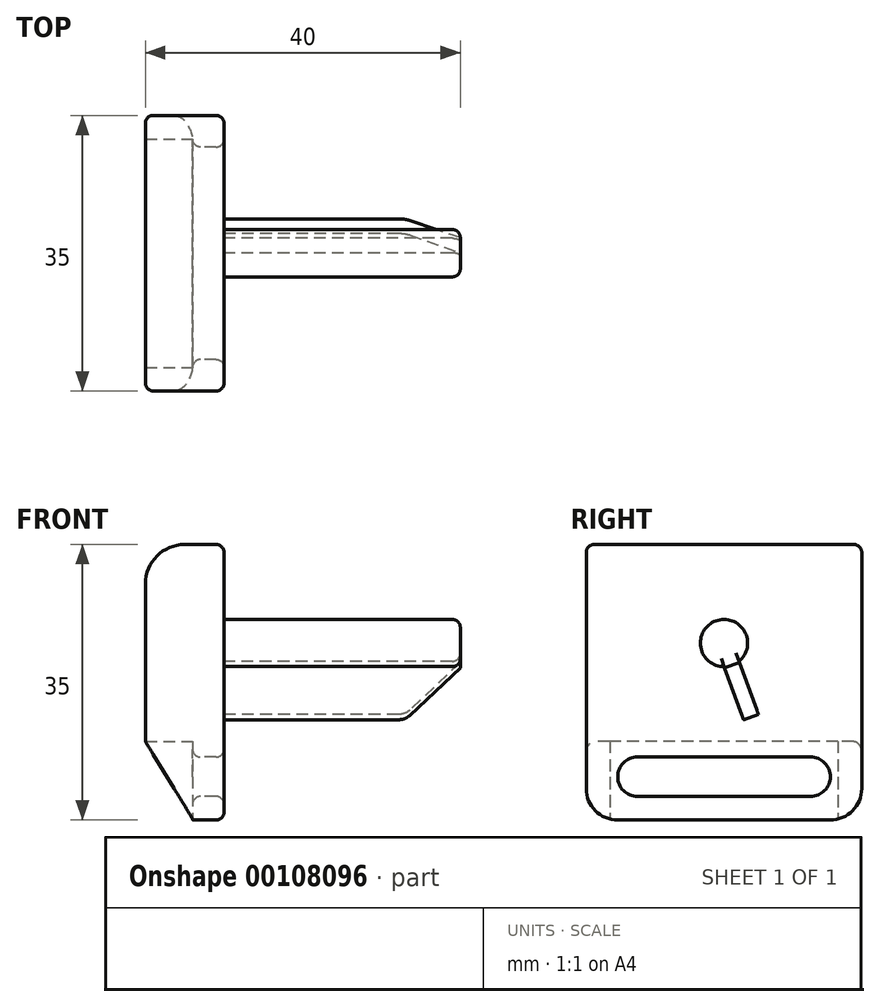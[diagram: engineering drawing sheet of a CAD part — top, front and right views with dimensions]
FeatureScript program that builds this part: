
annotation { "Feature Type Name" : "Feature", "Feature Type Description" : "" }
export const myFeature = defineFeature(function(context is Context, id is Id, definition is map)
    precondition{}
    {
        {
            var Q0;
            Q0=qCreatedBy(makeId("Right.planeOp"),FACE);
            var sketch = newSketch(context, id + "F0", { "sketchPlane" : qUnion([Q0])});
            skLineSegment(sketch, "E0.bottom", {"start": v(17.5, 12.5) * mm, "end": v(-17.5, 12.5) * mm});
            skLineSegment(sketch, "E0.top", {"start": v(17.5, -12.5) * mm, "end": v(-17.5, -12.5) * mm});
            skLineSegment(sketch, "E0.left", {"start": v(17.5, 12.5) * mm, "end": v(17.5, -12.5) * mm});
            skLineSegment(sketch, "E0.right", {"start": v(-17.5, 12.5) * mm, "end": v(-17.5, -12.5) * mm});
            skPoint(sketch, "E0.middle", {"position": v(0, 0) * mm});
            skSolve(sketch);
        }
        {
            var Q0;
            Q0 = qSketchRegion(id + "F0", true);
            extrude(context, id + "F1", {"entities" : qUnion([Q0]), "depth" : 6 * mm, "offsetDistance" : 25 * mm});
        }
        {
            var Q0;
            Q0=makeQuery(id+"F1.opExtrude","CAP_FACE",FACE,{"disambiguationData":[OSD([sQuery(id+"F0.wireOp",EDGE,"E0.bottom"),sQuery(id+"F0.wireOp",EDGE,"E0.top"),sQuery(id+"F0.wireOp",EDGE,"E0.left"),sQuery(id+"F0.wireOp",EDGE,"E0.right")])],"isStart":false});
            var sketch = newSketch(context, id + "F2", { "sketchPlane" : qUnion([Q0])});
            skPoint(sketch, "E1.0", {"position": v(-17.5, 12.5) * mm});
            skPoint(sketch, "E1.1", {"position": v(17.5, 12.5) * mm});
            skLineSegment(sketch, "E2.bottom", {"start": v(-17.5, 12.5) * mm, "end": v(17.5, 12.5) * mm});
            skLineSegment(sketch, "E2.top", {"start": v(-13.5, -22.5) * mm, "end": v(13.5, -22.5) * mm});
            skLineSegment(sketch, "E2.left", {"start": v(-17.5, 12.5) * mm, "end": v(-17.5, -18.5) * mm});
            skLineSegment(sketch, "E2.right", {"start": v(17.5, 12.5) * mm, "end": v(17.5, -18.5) * mm});
            skPoint(sketch, "E3.visualSharp", {"position": v(-17.5, -22.5) * mm});
            skArc(sketch, "E3.filletArc", {"start": v(-17.5, -18.5) * mm, "mid": v(-16.33, -21.33) * mm, "end": v(-13.5, -22.5) * mm});
            skPoint(sketch, "E4.visualSharp", {"position": v(17.5, -22.5) * mm});
            skArc(sketch, "E4.filletArc", {"start": v(13.5, -22.5) * mm, "mid": v(16.33, -21.33) * mm, "end": v(17.5, -18.5) * mm});
            skArc(sketch, "E5", {"start": v(-11, -14.5) * mm, "mid": v(-13.5, -17) * mm, "end": v(-11, -19.5) * mm});
            skArc(sketch, "E6.MirrorC", {"start": v(11, -14.5) * mm, "mid": v(13.5, -17) * mm, "end": v(11, -19.5) * mm});
            skLineSegment(sketch, "E7", {"start": v(-11, -14.5) * mm, "end": v(11, -14.5) * mm});
            skLineSegment(sketch, "E8", {"start": v(-11, -19.5) * mm, "end": v(11, -19.5) * mm});
            skSolve(sketch);
        }
        {
            var Q0;
            Q0 = qSketchRegion(id + "F2", true);
            extrude(context, id + "F3", {"entities" : qUnion([Q0]), "operationType" : NewBodyOperationType.ADD, "depth" : 4 * mm, "offsetDistance" : 25 * mm});
        }
        {
            var Q0;
            Q0=makeQuery(id+"F3.opExtrude","CAP_EDGE",EDGE,{"disambiguationData":[OSD([sQuery(id+"F2.wireOp",EDGE,"E3.filletArc")])],"isStart":false});
            var Q1;
            Q1=makeQuery(id+"F3.opExtrude","CAP_EDGE",EDGE,{"disambiguationData":[OSD([sQuery(id+"F2.wireOp",EDGE,"E8")])],"isStart":false});
            var Q2;
            Q2=makeQuery(id+"F3.opExtrude","CAP_EDGE",EDGE,{"disambiguationData":[OSD([sQuery(id+"F2.wireOp",EDGE,"E8")])],"isStart":true});
            fillet(context, id + "F4", {"entities" : qUnion([Q0, Q1, Q2]), "tangentPropagation" : true, "radius" : 1 * mm, "defaultsChanged" : false, "vertexSettings" : [], "allowEdgeOverflow" : false});
        }
        {
            var Q0;
            Q0=makeQuery(id+"F3.opExtrude","CAP_FACE",FACE,{"disambiguationData":[OSD([sQuery(id+"F2.wireOp",EDGE,"E2.bottom"),sQuery(id+"F2.wireOp",EDGE,"E2.top"),sQuery(id+"F2.wireOp",EDGE,"E2.left"),sQuery(id+"F2.wireOp",EDGE,"E2.right"),sQuery(id+"F2.wireOp",EDGE,"E3.filletArc"),sQuery(id+"F2.wireOp",EDGE,"E4.filletArc"),sQuery(id+"F2.wireOp",EDGE,"E5"),sQuery(id+"F2.wireOp",EDGE,"E6.MirrorC"),sQuery(id+"F2.wireOp",EDGE,"E7"),sQuery(id+"F2.wireOp",EDGE,"E8")])],"isStart":true});
            var sketch = newSketch(context, id + "F5", { "sketchPlane" : qUnion([Q0])});
            skLineSegment(sketch, "E9.0", {"start": v(-17.5, -12.5) * mm, "end": v(17.5, -12.5) * mm});
            skLineSegment(sketch, "E10.bottom", {"start": v(-17.5, -12.5) * mm, "end": v(-14.5, -12.5) * mm});
            skLineSegment(sketch, "E10.left", {"start": v(-17.5, -12.5) * mm, "end": v(-17.5, -18.5) * mm});
            skLineSegment(sketch, "E10.right", {"start": v(-14.5, -12.5) * mm, "end": v(-14.5, -22.37) * mm});
            skArc(sketch, "E11.0", {"start": v(-11, -20.5) * mm, "mid": v(-14.5, -17) * mm, "end": v(-11, -13.5) * mm, "construction": true});
            skArc(sketch, "E12.0", {"start": v(-14.5, -22.37) * mm, "mid": v(-16.66, -20.95) * mm, "end": v(-17.5, -18.5) * mm});
            skPoint(sketch, "E13.orphan", {"position": v(-13.5, -22.5) * mm});
            skPoint(sketch, "E14.MirrorP", {"position": v(13.5, -22.5) * mm});
            skLineSegment(sketch, "E15.MirrorCS", {"start": v(17.5, -12.5) * mm, "end": v(17.5, -18.5) * mm});
            skLineSegment(sketch, "E16.MirrorCS", {"start": v(14.5, -12.5) * mm, "end": v(14.5, -22.37) * mm});
            skLineSegment(sketch, "E17.MirrorCS", {"start": v(17.5, -12.5) * mm, "end": v(14.5, -12.5) * mm});
            skArc(sketch, "E18.MirrorCS", {"start": v(14.5, -22.37) * mm, "mid": v(16.66, -20.95) * mm, "end": v(17.5, -18.5) * mm});
            skSolve(sketch);
        }
        {
            var Q0;
            Q0 = qSketchRegion(id + "F5", true);
            var Q1;
            Q1=makeQuery(id+"F1.opExtrude","CAP_FACE",FACE,{"disambiguationData":[OSD([sQuery(id+"F0.wireOp",EDGE,"E0.bottom"),sQuery(id+"F0.wireOp",EDGE,"E0.top"),sQuery(id+"F0.wireOp",EDGE,"E0.left"),sQuery(id+"F0.wireOp",EDGE,"E0.right")])],"isStart":true});
            extrude(context, id + "F6", {"entities" : qUnion([Q0]), "operationType" : NewBodyOperationType.ADD, "endBound" : BoundingType.UP_TO_SURFACE, "depth" : 25 * mm, "endBoundEntityFace" : qUnion([Q1]), "offsetDistance" : 25 * mm});
        }
        {
            var Q0;
            Q0=makeQuery(id+"F6.boolean.opBoolean","MERGE",FACE,{"derivedFrom":[makeQuery(id+"F3.boolean.opBoolean","MERGE",FACE,{"derivedFrom":[makeQuery(id+"F1.opExtrude","SWEPT_FACE",FACE,{"disambiguationData":[OSD([sQuery(id+"F0.wireOp",EDGE,"E0.right")])]}),makeQuery(id+"F3.opExtrude","SWEPT_FACE",FACE,{"disambiguationData":[OSD([sQuery(id+"F2.wireOp",EDGE,"E2.left")])]})]}),makeQuery(id+"F6.opExtrude","SWEPT_FACE",FACE,{"disambiguationData":[OSD([sQuery(id+"F5.wireOp",EDGE,"E15.MirrorCS")])]})]});
            var sketch = newSketch(context, id + "F7", { "sketchPlane" : qUnion([Q0])});
            skLineSegment(sketch, "E19.0", {"start": v(0, -12.5) * mm, "end": v(6, -12.5) * mm, "construction": true});
            skLineSegment(sketch, "E20.0", {"start": v(6, -17) * mm, "end": v(6, -22.37) * mm, "construction": true});
            skPoint(sketch, "E21.0", {"position": v(0, -22.37) * mm});
            skLineSegment(sketch, "E22", {"start": v(0, -12.5) * mm, "end": v(6, -22.37) * mm});
            skLineSegment(sketch, "E23", {"start": v(0, -22.37) * mm, "end": v(0, -12.5) * mm});
            skLineSegment(sketch, "E24", {"start": v(0, -22.37) * mm, "end": v(6, -22.37) * mm});
            skSolve(sketch);
        }
        {
            var Q0;
            Q0 = qSketchRegion(id + "F7", true);
            extrude(context, id + "F8", {"entities" : qUnion([Q0]), "operationType" : NewBodyOperationType.REMOVE, "endBound" : BoundingType.THROUGH_ALL, "oppositeDirection" : true, "depth" : 25 * mm, "offsetDistance" : 25 * mm});
        }
        {
            var Q0;
            Q0=makeQuery(id+"F3.opExtrude","CAP_FACE",FACE,{"disambiguationData":[OSD([sQuery(id+"F2.wireOp",EDGE,"E2.bottom"),sQuery(id+"F2.wireOp",EDGE,"E2.top"),sQuery(id+"F2.wireOp",EDGE,"E2.left"),sQuery(id+"F2.wireOp",EDGE,"E2.right"),sQuery(id+"F2.wireOp",EDGE,"E3.filletArc"),sQuery(id+"F2.wireOp",EDGE,"E4.filletArc"),sQuery(id+"F2.wireOp",EDGE,"E5"),sQuery(id+"F2.wireOp",EDGE,"E6.MirrorC"),sQuery(id+"F2.wireOp",EDGE,"E7"),sQuery(id+"F2.wireOp",EDGE,"E8")])],"isStart":false});
            var sketch = newSketch(context, id + "F9", { "sketchPlane" : qUnion([Q0])});
            skArc(sketch, "E25", {"start": v(1.9, -2.33) * mm, "mid": v(-1.03, 2.8) * mm, "end": v(0.03, -3.02) * mm});
            skLineSegment(sketch, "E26", {"start": v(0, -0.02) * mm, "end": v(3.42, -9.42) * mm, "construction": true});
            skLineSegment(sketch, "E27.bottom", {"start": v(0, -0.02) * mm, "end": v(14.41, -0.02) * mm, "construction": true});
            skLineSegment(sketch, "E27.top", {"start": v(0, -0.02) * mm, "end": v(14.41, -0.02) * mm, "construction": true});
            skLineSegment(sketch, "E27.left", {"start": v(0, -0.02) * mm, "end": v(0, -0.02) * mm});
            skLineSegment(sketch, "E27.right", {"start": v(14.41, -0.02) * mm, "end": v(14.41, -0.02) * mm});
            skLineSegment(sketch, "E28", {"start": v(1.9, -2.33) * mm, "end": v(4.36, -9.07) * mm});
            skLineSegment(sketch, "E29.MirrorCS", {"start": v(0.03, -3.02) * mm, "end": v(2.48, -9.76) * mm});
            skPoint(sketch, "E30.orphan", {"position": v(2.35, -3.56) * mm});
            skPoint(sketch, "E31.orphan", {"position": v(0.47, -4.24) * mm});
            skLineSegment(sketch, "E32", {"start": v(2.48, -9.76) * mm, "end": v(4.36, -9.07) * mm});
            skSolve(sketch);
        }
        {
            var Q0;
            Q0 = qSketchRegion(id + "F9", true);
            extrude(context, id + "F10", {"entities" : qUnion([Q0]), "operationType" : NewBodyOperationType.ADD, "depth" : 30 * mm, "offsetDistance" : 25 * mm});
        }
        {
            var Q0;
            Q0=makeQuery(id+"F10.opExtrude","CAP_EDGE",EDGE,{"disambiguationData":[OSD([sQuery(id+"F9.wireOp",EDGE,"E32")])],"isStart":false});
            chamfer(context, id + "F11", {"entities" : qUnion([Q0]), "width" : 7 * mm, "tangentPropagation" : true});
        }
        {
            var Q0;
            {var subQ0=sQuery(id+"F9.wireOp",EDGE,"3ov4aeCL-emDo-Vj3k-tZrB-0FQBTPLo7AsV");Q0=makeQuery(id+"F11.opChamfer","BLEND_EDGE",EDGE,{"blendedFrom":[makeQuery(id+"F10.opExtrude","CAP_EDGE",EDGE,{"disambiguationData":[OSD([subQ0])],"isStart":false}),makeQuery(id+"F10.opExtrude","SWEPT_FACE",FACE,{"disambiguationData":[OSD([subQ0])]})],"blendedInto":[makeQuery(id+"F10.opExtrude","SWEPT_FACE",FACE,{"disambiguationData":[OSD([subQ0])]})]});}
            var Q1;
            {var subQ0=sQuery(id+"F9.wireOp",EDGE,"E32");Q1=makeQuery(id+"F11.opChamfer","BLEND_EDGE",EDGE,{"blendedFrom":[makeQuery(id+"F10.opExtrude","CAP_EDGE",EDGE,{"disambiguationData":[OSD([subQ0])],"isStart":false}),makeQuery(id+"F10.opExtrude","SWEPT_FACE",FACE,{"disambiguationData":[OSD([subQ0])]})],"blendedInto":[makeQuery(id+"F10.opExtrude","SWEPT_FACE",FACE,{"disambiguationData":[OSD([subQ0])]})]});}
            fillet(context, id + "F12", {"entities" : qUnion([Q0, Q1]), "tangentPropagation" : true, "radius" : 2 * mm, "defaultsChanged" : false, "vertexSettings" : [], "allowEdgeOverflow" : false});
        }
        {
            var Q0;
            Q0=makeQuery(id+"F1.opExtrude","CAP_EDGE",EDGE,{"disambiguationData":[OSD([sQuery(id+"F0.wireOp",EDGE,"E0.bottom")])],"isStart":true});
            fillet(context, id + "F13", {"entities" : qUnion([Q0]), "tangentPropagation" : true, "radius" : 5 * mm, "defaultsChanged" : false, "vertexSettings" : [], "allowEdgeOverflow" : false});
        }
        {
            var Q0;
            Q0=makeQuery(id+"F6.boolean.opBoolean","MERGE",EDGE,{"derivedFrom":[makeQuery(id+"F1.opExtrude","CAP_EDGE",EDGE,{"disambiguationData":[OSD([sQuery(id+"F0.wireOp",EDGE,"E0.left")])],"isStart":true}),makeQuery(id+"F6.opExtrude","CAP_EDGE",EDGE,{"disambiguationData":[OSD([sQuery(id+"F5.wireOp",EDGE,"E10.left")])],"isStart":false})]});
            fillet(context, id + "F14", {"entities" : qUnion([Q0]), "tangentPropagation" : true, "radius" : 1 * mm, "defaultsChanged" : false, "vertexSettings" : [], "allowEdgeOverflow" : false});
        }
        {
            var Q0;
            Q0=makeQuery(id+"F10.opExtrude","CAP_EDGE",EDGE,{"disambiguationData":[OSD([sQuery(id+"F9.wireOp",EDGE,"E28")])],"isStart":true});
            var Q1;
            Q1=makeQuery(id+"F10.opExtrude","CAP_EDGE",EDGE,{"disambiguationData":[OSD([sQuery(id+"F9.wireOp",EDGE,"E25")])],"isStart":true});
            var Q2;
            Q2=makeQuery(id+"F10.opExtrude","CAP_EDGE",EDGE,{"disambiguationData":[OSD([sQuery(id+"F9.wireOp",EDGE,"E32")])],"isStart":true});
            var Q3;
            Q3=makeQuery(id+"F10.opExtrude","CAP_EDGE",EDGE,{"disambiguationData":[OSD([sQuery(id+"F9.wireOp",EDGE,"E29.MirrorCS")])],"isStart":true});
            var Q4;
            Q4=makeQuery(id+"F10.opExtrude","CAP_EDGE",EDGE,{"disambiguationData":[OSD([sQuery(id+"F9.wireOp",EDGE,"E25")])],"isStart":false});
            fillet(context, id + "F15", {"entities" : qUnion([Q0, Q1, Q2, Q3, Q4]), "tangentPropagation" : true, "radius" : 1 * mm, "defaultsChanged" : false, "vertexSettings" : [], "allowEdgeOverflow" : false});
        }
    });
